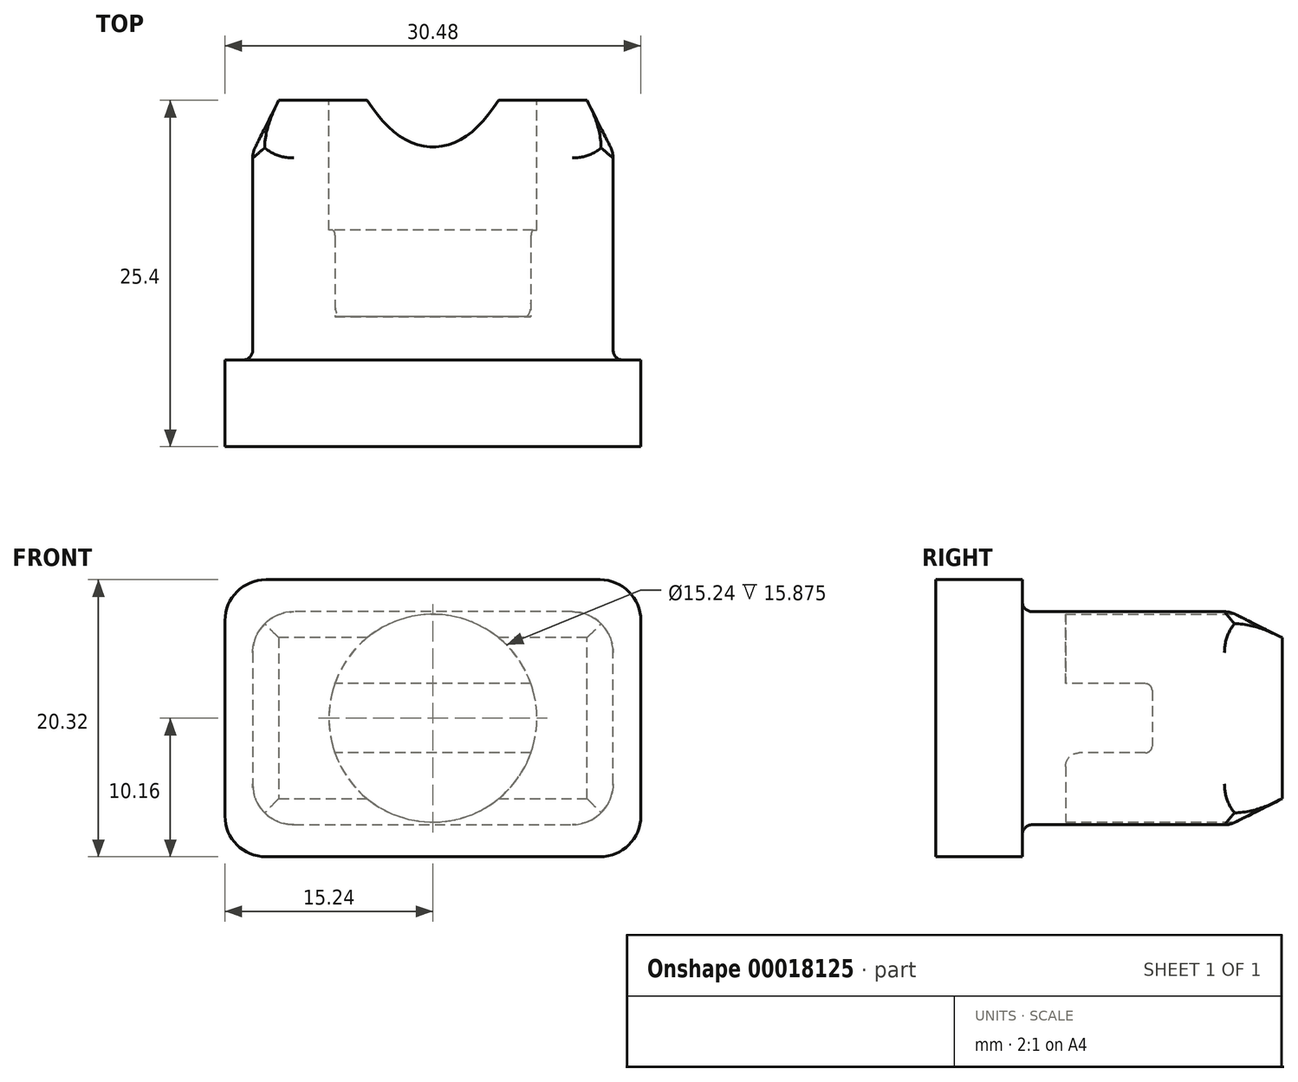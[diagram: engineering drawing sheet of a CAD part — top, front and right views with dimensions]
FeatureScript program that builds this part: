
annotation { "Feature Type Name" : "Feature", "Feature Type Description" : "" }
export const myFeature = defineFeature(function(context is Context, id is Id, definition is map)
    precondition{}
    {
        {
            var Q0;
            Q0=qCreatedBy(makeId("Front.planeOp"),FACE);
            var sketch = newSketch(context, id + "F0", { "sketchPlane" : qUnion([Q0])});
            skLineSegment(sketch, "E0.bottom", {"start": v(0, 0) * mm, "end": v(30.48, 0) * mm});
            skLineSegment(sketch, "E0.top", {"start": v(0, 20.32) * mm, "end": v(30.48, 20.32) * mm});
            skLineSegment(sketch, "E0.left", {"start": v(0, 0) * mm, "end": v(0, 20.32) * mm});
            skLineSegment(sketch, "E0.right", {"start": v(30.48, 0) * mm, "end": v(30.48, 20.32) * mm});
            skSolve(sketch);
        }
        {
            var Q0;
            Q0=makeQuery(id+"F0.imprint","IMPRINT",FACE,{"disambiguationData":[TD([[makeQuery(id+"F0.imprint","IMPRINT",EDGE,{"derivedFrom":sQuery(id+"F0.wireOp",EDGE,"E0.bottom")}),1.0]])]});
            extrude(context, id + "F1", {"entities" : qUnion([Q0]), "oppositeDirection" : true, "depth" : 6.34 * mm});
        }
        {
            var Q0;
            Q0=makeQuery(id+"F1.opExtrude","CAP_FACE",FACE,{"disambiguationData":[OSD([sQuery(id+"F0.wireOp",EDGE,"E0.bottom"),sQuery(id+"F0.wireOp",EDGE,"E0.top"),sQuery(id+"F0.wireOp",EDGE,"E0.left"),sQuery(id+"F0.wireOp",EDGE,"E0.right")])],"isStart":false});
            var sketch = newSketch(context, id + "F2", { "sketchPlane" : qUnion([Q0])});
            skLineSegment(sketch, "E1.bottom", {"start": v(-2.03, 2.35) * mm, "end": v(-28.45, 2.35) * mm});
            skLineSegment(sketch, "E1.top", {"start": v(-2.03, 17.97) * mm, "end": v(-28.45, 17.97) * mm});
            skLineSegment(sketch, "E1.left", {"start": v(-2.03, 2.35) * mm, "end": v(-2.03, 17.97) * mm});
            skLineSegment(sketch, "E1.right", {"start": v(-28.45, 2.35) * mm, "end": v(-28.45, 17.97) * mm});
            skLineSegment(sketch, "E2", {"start": v(-15.24, 20.32) * mm, "end": v(-15.24, 0) * mm, "construction": true});
            skLineSegment(sketch, "E3", {"start": v(-30.48, 10.16) * mm, "end": v(0, 10.16) * mm, "construction": true});
            skSolve(sketch);
        }
        {
            var Q0;
            Q0=makeQuery(id+"F2.imprint","IMPRINT",FACE,{"disambiguationData":[TD([[makeQuery(id+"F2.imprint","IMPRINT",EDGE,{"derivedFrom":sQuery(id+"F2.wireOp",EDGE,"E1.bottom")}),-1.0]])]});
            extrude(context, id + "F3", {"entities" : qUnion([Q0]), "operationType" : NewBodyOperationType.ADD, "depth" : 19.05 * mm});
        }
        {
            var Q0;
            Q0=makeQuery(id+"F3.opExtrude","CAP_FACE",FACE,{"disambiguationData":[OSD([sQuery(id+"F2.wireOp",EDGE,"E1.bottom"),sQuery(id+"F2.wireOp",EDGE,"E1.top"),sQuery(id+"F2.wireOp",EDGE,"E1.left"),sQuery(id+"F2.wireOp",EDGE,"E1.right")])],"isStart":false});
            var sketch = newSketch(context, id + "F4", { "sketchPlane" : qUnion([Q0])});
            skCircle(sketch, "E4", {"center": v(-15.24, 10.16) * mm, "radius": 7.62 * mm});
            skLineSegment(sketch, "E5", {"start": v(-30.48, 10.16) * mm, "end": v(0, 10.16) * mm, "construction": true});
            skLineSegment(sketch, "E6", {"start": v(-15.24, 20.32) * mm, "end": v(-15.24, 0) * mm, "construction": true});
            skSolve(sketch);
        }
        {
            var Q0;
            Q0=makeQuery(id+"F4.imprint","IMPRINT",FACE,{"disambiguationData":[TD([[makeQuery(id+"F4.imprint","IMPRINT",EDGE,{"derivedFrom":sQuery(id+"F4.wireOp",EDGE,"E4")}),1.0]])]});
            extrude(context, id + "F5", {"entities" : qUnion([Q0]), "operationType" : NewBodyOperationType.REMOVE, "oppositeDirection" : true, "depth" : 15.88 * mm});
        }
        {
            var Q0;
            Q0=makeQuery(id+"F1.opExtrude","SWEPT_EDGE",EDGE,{"disambiguationData":[OSD([sQuery(id+"F0.wireOp",EDGE,"E0.top"),sQuery(id+"F0.wireOp",EDGE,"E0.left")])]});
            var Q1;
            Q1=makeQuery(id+"F1.opExtrude","SWEPT_EDGE",EDGE,{"disambiguationData":[OSD([sQuery(id+"F0.wireOp",EDGE,"E0.top"),sQuery(id+"F0.wireOp",EDGE,"E0.right")])]});
            var Q2;
            Q2=makeQuery(id+"F1.opExtrude","SWEPT_EDGE",EDGE,{"disambiguationData":[OSD([sQuery(id+"F0.wireOp",EDGE,"E0.bottom"),sQuery(id+"F0.wireOp",EDGE,"E0.right")])]});
            var Q3;
            Q3=makeQuery(id+"F1.opExtrude","SWEPT_EDGE",EDGE,{"disambiguationData":[OSD([sQuery(id+"F0.wireOp",EDGE,"E0.bottom"),sQuery(id+"F0.wireOp",EDGE,"E0.left")])]});
            fillet(context, id + "F6", {"entities" : qUnion([Q0, Q1, Q2, Q3]), "radius" : 3 * mm, "tangentPropagation" : true, "allowEdgeOverflow" : false});
        }
        {
            var Q0;
            Q0=makeQuery(id+"F3.opExtrude","SWEPT_FACE",FACE,{"disambiguationData":[OSD([sQuery(id+"F2.wireOp",EDGE,"E1.top")])]});
            var sketch = newSketch(context, id + "F7", { "sketchPlane" : qUnion([Q0])});
            skLineSegment(sketch, "E7", {"start": v(2.03, 21.59) * mm, "end": v(3.94, 25.4) * mm});
            skSolve(sketch);
        }
        {
            var Q0;
            {var subQ2=sQuery(id+"F7.wireOp",EDGE,"E7");Q0=makeQuery(id+"F7.imprint","IMPRINT",FACE,{"disambiguationData":[TD([[makeQuery(id+"F7.imprint","IMPRINT",EDGE,{"derivedFrom":subQ2}),1.0]])]});}
            var Q1;
            Q1=makeQuery(id+"F3.opExtrude","CAP_EDGE",EDGE,{"disambiguationData":[OSD([sQuery(id+"F2.wireOp",EDGE,"E1.left")])],"isStart":false});
            var Q2;
            Q2=makeQuery(id+"F3.opExtrude","CAP_EDGE",EDGE,{"disambiguationData":[OSD([sQuery(id+"F2.wireOp",EDGE,"E1.bottom")])],"isStart":false});
            var Q3;
            Q3=makeQuery(id+"F3.opExtrude","CAP_EDGE",EDGE,{"disambiguationData":[OSD([sQuery(id+"F2.wireOp",EDGE,"E1.right")])],"isStart":false});
            var Q4;
            Q4=makeQuery(id+"F3.opExtrude","CAP_EDGE",EDGE,{"disambiguationData":[OSD([sQuery(id+"F2.wireOp",EDGE,"E1.top")])],"isStart":false});
            sweep(context, id + "F8", {"operationType" : NewBodyOperationType.REMOVE, "profiles" : qUnion([Q0]), "path" : qUnion([Q1, Q2, Q3, Q4])});
        }
        {
            var Q0;
            Q0=makeQuery(id+"F3.opExtrude","SWEPT_EDGE",EDGE,{"disambiguationData":[OSD([sQuery(id+"F2.wireOp",EDGE,"E1.top"),sQuery(id+"F2.wireOp",EDGE,"E1.right")])]});
            var Q1;
            Q1=makeQuery(id+"F3.opExtrude","SWEPT_EDGE",EDGE,{"disambiguationData":[OSD([sQuery(id+"F2.wireOp",EDGE,"E1.bottom"),sQuery(id+"F2.wireOp",EDGE,"E1.right")])]});
            var Q2;
            Q2=makeQuery(id+"F3.opExtrude","SWEPT_EDGE",EDGE,{"disambiguationData":[OSD([sQuery(id+"F2.wireOp",EDGE,"E1.top"),sQuery(id+"F2.wireOp",EDGE,"E1.left")])]});
            var Q3;
            Q3=makeQuery(id+"F3.opExtrude","SWEPT_EDGE",EDGE,{"disambiguationData":[OSD([sQuery(id+"F2.wireOp",EDGE,"E1.bottom"),sQuery(id+"F2.wireOp",EDGE,"E1.left")])]});
            fillet(context, id + "F9", {"entities" : qUnion([Q0, Q1, Q2, Q3]), "radius" : 3 * mm, "tangentPropagation" : true, "allowEdgeOverflow" : false});
        }
        {
            var Q0;
            Q0=makeQuery(id+"F5.boolean.opBoolean","COPY",FACE,{"derivedFrom":makeQuery(id+"F5.opExtrude","CAP_FACE",FACE,{"disambiguationData":[OSD([sQuery(id+"F4.wireOp",EDGE,"E4")])],"isStart":false})});
            var sketch = newSketch(context, id + "F10", { "sketchPlane" : qUnion([Q0])});
            skLineSegment(sketch, "E8", {"start": v(-7.62, 10.16) * mm, "end": v(-22.86, 10.16) * mm, "construction": true});
            skPoint(sketch, "E9", {"position": v(-15.24, 10.16) * mm});
            skLineSegment(sketch, "E10", {"start": v(-15.24, 2.54) * mm, "end": v(-15.24, 17.78) * mm, "construction": true});
            skLineSegment(sketch, "E11.bottom", {"start": v(-22.86, 12.7) * mm, "end": v(-7.62, 12.7) * mm});
            skLineSegment(sketch, "E11.top", {"start": v(-22.86, 7.62) * mm, "end": v(-7.62, 7.62) * mm});
            skLineSegment(sketch, "E11.left", {"start": v(-22.86, 12.7) * mm, "end": v(-22.86, 7.62) * mm});
            skLineSegment(sketch, "E11.right", {"start": v(-7.62, 12.7) * mm, "end": v(-7.62, 7.62) * mm});
            skSolve(sketch);
        }
        {
            var Q0;
            {var subQ0=makeQuery(id+"F5.boolean.opBoolean","COPY",EDGE,{"derivedFrom":makeQuery(id+"F5.opExtrude","CAP_EDGE",EDGE,{"disambiguationData":[OSD([sQuery(id+"F4.wireOp",EDGE,"E4")])],"isStart":false})});var subQ6=sQuery(id+"F10.wireOp",EDGE,"E11.bottom");var subQ8=makeQuery(id+"F10.imprint","INTERSECT",VERTEX,{"disambiguationData":[OD(0.0)],"derivedFrom":[subQ0,subQ6]});Q0=makeQuery(id+"F10.imprint","IMPRINT",FACE,{"disambiguationData":[TD([[makeQuery(id+"F10.imprint","IMPRINT",EDGE,{"disambiguationData":[TD([[subQ8,-1.0]])],"derivedFrom":subQ6}),-1.0]])]});}
            extrude(context, id + "F11", {"entities" : qUnion([Q0]), "operationType" : NewBodyOperationType.ADD, "depth" : 6.35 * mm});
        }
        {
            var Q0;
            Q0=makeQuery(id+"F11.opExtrude","CAP_EDGE",EDGE,{"disambiguationData":[OSD([sQuery(id+"F10.wireOp",EDGE,"E11.bottom")])],"isStart":false});
            var Q1;
            Q1=makeQuery(id+"F11.opExtrude","CAP_EDGE",EDGE,{"disambiguationData":[OSD([sQuery(id+"F10.wireOp",EDGE,"E11.top")])],"isStart":false});
            fillet(context, id + "F12", {"entities" : qUnion([Q0, Q1]), "radius" : 0.5 * mm, "tangentPropagation" : true, "allowEdgeOverflow" : false});
        }
        {
            var Q0;
            Q0=makeQuery(id+"F11.opExtrude","CAP_EDGE",EDGE,{"disambiguationData":[OSD([sQuery(id+"F10.wireOp",EDGE,"E11.bottom")])],"isStart":true});
            var Q1;
            Q1=makeQuery(id+"F11.opExtrude","CAP_EDGE",EDGE,{"disambiguationData":[OSD([sQuery(id+"F10.wireOp",EDGE,"E11.top")])],"isStart":true});
            fillet(context, id + "F13", {"entities" : qUnion([Q0, Q1]), "radius" : 1 * mm, "tangentPropagation" : true, "allowEdgeOverflow" : false});
        }
        {
            var Q0;
            Q0=makeQuery(id+"F3.opExtrude","CAP_EDGE",EDGE,{"disambiguationData":[OSD([sQuery(id+"F2.wireOp",EDGE,"E1.top")])],"isStart":true});
            var Q1;
            Q1=makeQuery(id+"F9.opFillet","BLEND_EDGE",EDGE,{"blendedFrom":[makeQuery(id+"F3.opExtrude","SWEPT_EDGE",EDGE,{"disambiguationData":[OSD([sQuery(id+"F2.wireOp",EDGE,"E1.top"),sQuery(id+"F2.wireOp",EDGE,"E1.right")])]}),makeQuery(id+"F1.opExtrude","CAP_FACE",FACE,{"disambiguationData":[OSD([sQuery(id+"F0.wireOp",EDGE,"E0.bottom"),sQuery(id+"F0.wireOp",EDGE,"E0.top"),sQuery(id+"F0.wireOp",EDGE,"E0.left"),sQuery(id+"F0.wireOp",EDGE,"E0.right")])],"isStart":false})],"blendedInto":[makeQuery(id+"F1.opExtrude","CAP_FACE",FACE,{"disambiguationData":[OSD([sQuery(id+"F0.wireOp",EDGE,"E0.bottom"),sQuery(id+"F0.wireOp",EDGE,"E0.top"),sQuery(id+"F0.wireOp",EDGE,"E0.left"),sQuery(id+"F0.wireOp",EDGE,"E0.right")])],"isStart":false})]});
            var Q2;
            Q2=makeQuery(id+"F3.opExtrude","CAP_EDGE",EDGE,{"disambiguationData":[OSD([sQuery(id+"F2.wireOp",EDGE,"E1.right")])],"isStart":true});
            var Q3;
            Q3=makeQuery(id+"F9.opFillet","BLEND_EDGE",EDGE,{"blendedFrom":[makeQuery(id+"F3.opExtrude","SWEPT_EDGE",EDGE,{"disambiguationData":[OSD([sQuery(id+"F2.wireOp",EDGE,"E1.bottom"),sQuery(id+"F2.wireOp",EDGE,"E1.right")])]}),makeQuery(id+"F1.opExtrude","CAP_FACE",FACE,{"disambiguationData":[OSD([sQuery(id+"F0.wireOp",EDGE,"E0.bottom"),sQuery(id+"F0.wireOp",EDGE,"E0.top"),sQuery(id+"F0.wireOp",EDGE,"E0.left"),sQuery(id+"F0.wireOp",EDGE,"E0.right")])],"isStart":false})],"blendedInto":[makeQuery(id+"F1.opExtrude","CAP_FACE",FACE,{"disambiguationData":[OSD([sQuery(id+"F0.wireOp",EDGE,"E0.bottom"),sQuery(id+"F0.wireOp",EDGE,"E0.top"),sQuery(id+"F0.wireOp",EDGE,"E0.left"),sQuery(id+"F0.wireOp",EDGE,"E0.right")])],"isStart":false})]});
            var Q4;
            Q4=makeQuery(id+"F3.opExtrude","CAP_EDGE",EDGE,{"disambiguationData":[OSD([sQuery(id+"F2.wireOp",EDGE,"E1.bottom")])],"isStart":true});
            var Q5;
            Q5=makeQuery(id+"F9.opFillet","BLEND_EDGE",EDGE,{"blendedFrom":[makeQuery(id+"F3.opExtrude","SWEPT_EDGE",EDGE,{"disambiguationData":[OSD([sQuery(id+"F2.wireOp",EDGE,"E1.bottom"),sQuery(id+"F2.wireOp",EDGE,"E1.left")])]}),makeQuery(id+"F1.opExtrude","CAP_FACE",FACE,{"disambiguationData":[OSD([sQuery(id+"F0.wireOp",EDGE,"E0.bottom"),sQuery(id+"F0.wireOp",EDGE,"E0.top"),sQuery(id+"F0.wireOp",EDGE,"E0.left"),sQuery(id+"F0.wireOp",EDGE,"E0.right")])],"isStart":false})],"blendedInto":[makeQuery(id+"F1.opExtrude","CAP_FACE",FACE,{"disambiguationData":[OSD([sQuery(id+"F0.wireOp",EDGE,"E0.bottom"),sQuery(id+"F0.wireOp",EDGE,"E0.top"),sQuery(id+"F0.wireOp",EDGE,"E0.left"),sQuery(id+"F0.wireOp",EDGE,"E0.right")])],"isStart":false})]});
            var Q6;
            Q6=makeQuery(id+"F3.opExtrude","CAP_EDGE",EDGE,{"disambiguationData":[OSD([sQuery(id+"F2.wireOp",EDGE,"E1.left")])],"isStart":true});
            var Q7;
            Q7=makeQuery(id+"F9.opFillet","BLEND_EDGE",EDGE,{"blendedFrom":[makeQuery(id+"F3.opExtrude","SWEPT_EDGE",EDGE,{"disambiguationData":[OSD([sQuery(id+"F2.wireOp",EDGE,"E1.top"),sQuery(id+"F2.wireOp",EDGE,"E1.left")])]}),makeQuery(id+"F1.opExtrude","CAP_FACE",FACE,{"disambiguationData":[OSD([sQuery(id+"F0.wireOp",EDGE,"E0.bottom"),sQuery(id+"F0.wireOp",EDGE,"E0.top"),sQuery(id+"F0.wireOp",EDGE,"E0.left"),sQuery(id+"F0.wireOp",EDGE,"E0.right")])],"isStart":false})],"blendedInto":[makeQuery(id+"F1.opExtrude","CAP_FACE",FACE,{"disambiguationData":[OSD([sQuery(id+"F0.wireOp",EDGE,"E0.bottom"),sQuery(id+"F0.wireOp",EDGE,"E0.top"),sQuery(id+"F0.wireOp",EDGE,"E0.left"),sQuery(id+"F0.wireOp",EDGE,"E0.right")])],"isStart":false})]});
            fillet(context, id + "F14", {"entities" : qUnion([Q0, Q1, Q2, Q3, Q4, Q5, Q6, Q7]), "radius" : 0.75 * mm, "tangentPropagation" : true, "allowEdgeOverflow" : false});
        }
        {
            var Q0;
            {var subQ0=sQuery(id+"F2.wireOp",EDGE,"E1.left");Q0=makeQuery(id+"F9.opFillet","BLEND_EDGE",EDGE,{"blendedFrom":[makeQuery(id+"F3.opExtrude","SWEPT_EDGE",EDGE,{"disambiguationData":[OSD([sQuery(id+"F2.wireOp",EDGE,"E1.top"),subQ0])]}),makeQuery(id+"F8.boolean.opBoolean","COPY",FACE,{"derivedFrom":makeQuery(id+"F8.opSweep","SWEPT_FACE",FACE,{"disambiguationData":[OSD([subQ0,sQuery(id+"F7.wireOp",EDGE,"E7")])]})})],"blendedInto":[makeQuery(id+"F8.boolean.opBoolean","COPY",FACE,{"derivedFrom":makeQuery(id+"F8.opSweep","SWEPT_FACE",FACE,{"disambiguationData":[OSD([subQ0,sQuery(id+"F7.wireOp",EDGE,"E7")])]})})]});}
            var Q1;
            {var subQ0=sQuery(id+"F2.wireOp",EDGE,"E1.top");Q1=makeQuery(id+"F9.opFillet","BLEND_EDGE",EDGE,{"blendedFrom":[makeQuery(id+"F3.opExtrude","SWEPT_EDGE",EDGE,{"disambiguationData":[OSD([subQ0,sQuery(id+"F2.wireOp",EDGE,"E1.left")])]}),makeQuery(id+"F8.boolean.opBoolean","COPY",FACE,{"derivedFrom":makeQuery(id+"F8.opSweep","SWEPT_FACE",FACE,{"disambiguationData":[OSD([subQ0,sQuery(id+"F7.wireOp",EDGE,"E7")])]})})],"blendedInto":[makeQuery(id+"F8.boolean.opBoolean","COPY",FACE,{"derivedFrom":makeQuery(id+"F8.opSweep","SWEPT_FACE",FACE,{"disambiguationData":[OSD([subQ0,sQuery(id+"F7.wireOp",EDGE,"E7")])]})})]});}
            var Q2;
            {var subQ0=sQuery(id+"F2.wireOp",EDGE,"E1.left");Q2=makeQuery(id+"F9.opFillet","BLEND_EDGE",EDGE,{"blendedFrom":[makeQuery(id+"F3.opExtrude","SWEPT_EDGE",EDGE,{"disambiguationData":[OSD([sQuery(id+"F2.wireOp",EDGE,"E1.bottom"),subQ0])]}),makeQuery(id+"F8.boolean.opBoolean","COPY",FACE,{"derivedFrom":makeQuery(id+"F8.opSweep","SWEPT_FACE",FACE,{"disambiguationData":[OSD([subQ0,sQuery(id+"F7.wireOp",EDGE,"E7")])]})})],"blendedInto":[makeQuery(id+"F8.boolean.opBoolean","COPY",FACE,{"derivedFrom":makeQuery(id+"F8.opSweep","SWEPT_FACE",FACE,{"disambiguationData":[OSD([subQ0,sQuery(id+"F7.wireOp",EDGE,"E7")])]})})]});}
            var Q3;
            {var subQ0=sQuery(id+"F2.wireOp",EDGE,"E1.bottom");Q3=makeQuery(id+"F9.opFillet","BLEND_EDGE",EDGE,{"blendedFrom":[makeQuery(id+"F3.opExtrude","SWEPT_EDGE",EDGE,{"disambiguationData":[OSD([subQ0,sQuery(id+"F2.wireOp",EDGE,"E1.left")])]}),makeQuery(id+"F8.boolean.opBoolean","COPY",FACE,{"derivedFrom":makeQuery(id+"F8.opSweep","SWEPT_FACE",FACE,{"disambiguationData":[OSD([subQ0,sQuery(id+"F7.wireOp",EDGE,"E7")])]})})],"blendedInto":[makeQuery(id+"F8.boolean.opBoolean","COPY",FACE,{"derivedFrom":makeQuery(id+"F8.opSweep","SWEPT_FACE",FACE,{"disambiguationData":[OSD([subQ0,sQuery(id+"F7.wireOp",EDGE,"E7")])]})})]});}
            var Q4;
            {var subQ0=sQuery(id+"F2.wireOp",EDGE,"E1.top");Q4=makeQuery(id+"F9.opFillet","BLEND_EDGE",EDGE,{"blendedFrom":[makeQuery(id+"F3.opExtrude","SWEPT_EDGE",EDGE,{"disambiguationData":[OSD([subQ0,sQuery(id+"F2.wireOp",EDGE,"E1.right")])]}),makeQuery(id+"F8.boolean.opBoolean","COPY",FACE,{"derivedFrom":makeQuery(id+"F8.opSweep","SWEPT_FACE",FACE,{"disambiguationData":[OSD([subQ0,sQuery(id+"F7.wireOp",EDGE,"E7")])]})})],"blendedInto":[makeQuery(id+"F8.boolean.opBoolean","COPY",FACE,{"derivedFrom":makeQuery(id+"F8.opSweep","SWEPT_FACE",FACE,{"disambiguationData":[OSD([subQ0,sQuery(id+"F7.wireOp",EDGE,"E7")])]})})]});}
            var Q5;
            {var subQ0=sQuery(id+"F2.wireOp",EDGE,"E1.right");Q5=makeQuery(id+"F9.opFillet","BLEND_EDGE",EDGE,{"blendedFrom":[makeQuery(id+"F3.opExtrude","SWEPT_EDGE",EDGE,{"disambiguationData":[OSD([sQuery(id+"F2.wireOp",EDGE,"E1.top"),subQ0])]}),makeQuery(id+"F8.boolean.opBoolean","COPY",FACE,{"derivedFrom":makeQuery(id+"F8.opSweep","SWEPT_FACE",FACE,{"disambiguationData":[OSD([subQ0,sQuery(id+"F7.wireOp",EDGE,"E7")])]})})],"blendedInto":[makeQuery(id+"F8.boolean.opBoolean","COPY",FACE,{"derivedFrom":makeQuery(id+"F8.opSweep","SWEPT_FACE",FACE,{"disambiguationData":[OSD([subQ0,sQuery(id+"F7.wireOp",EDGE,"E7")])]})})]});}
            var Q6;
            {var subQ0=sQuery(id+"F2.wireOp",EDGE,"E1.right");Q6=makeQuery(id+"F9.opFillet","BLEND_EDGE",EDGE,{"blendedFrom":[makeQuery(id+"F3.opExtrude","SWEPT_EDGE",EDGE,{"disambiguationData":[OSD([sQuery(id+"F2.wireOp",EDGE,"E1.bottom"),subQ0])]}),makeQuery(id+"F8.boolean.opBoolean","COPY",FACE,{"derivedFrom":makeQuery(id+"F8.opSweep","SWEPT_FACE",FACE,{"disambiguationData":[OSD([subQ0,sQuery(id+"F7.wireOp",EDGE,"E7")])]})})],"blendedInto":[makeQuery(id+"F8.boolean.opBoolean","COPY",FACE,{"derivedFrom":makeQuery(id+"F8.opSweep","SWEPT_FACE",FACE,{"disambiguationData":[OSD([subQ0,sQuery(id+"F7.wireOp",EDGE,"E7")])]})})]});}
            var Q7;
            {var subQ0=sQuery(id+"F2.wireOp",EDGE,"E1.bottom");Q7=makeQuery(id+"F9.opFillet","BLEND_EDGE",EDGE,{"blendedFrom":[makeQuery(id+"F3.opExtrude","SWEPT_EDGE",EDGE,{"disambiguationData":[OSD([subQ0,sQuery(id+"F2.wireOp",EDGE,"E1.right")])]}),makeQuery(id+"F8.boolean.opBoolean","COPY",FACE,{"derivedFrom":makeQuery(id+"F8.opSweep","SWEPT_FACE",FACE,{"disambiguationData":[OSD([subQ0,sQuery(id+"F7.wireOp",EDGE,"E7")])]})})],"blendedInto":[makeQuery(id+"F8.boolean.opBoolean","COPY",FACE,{"derivedFrom":makeQuery(id+"F8.opSweep","SWEPT_FACE",FACE,{"disambiguationData":[OSD([subQ0,sQuery(id+"F7.wireOp",EDGE,"E7")])]})})]});}
            fillet(context, id + "F15", {"entities" : qUnion([Q0, Q1, Q2, Q3, Q4, Q5, Q6, Q7]), "radius" : 1.75 * mm, "tangentPropagation" : true, "allowEdgeOverflow" : false});
        }
    });
